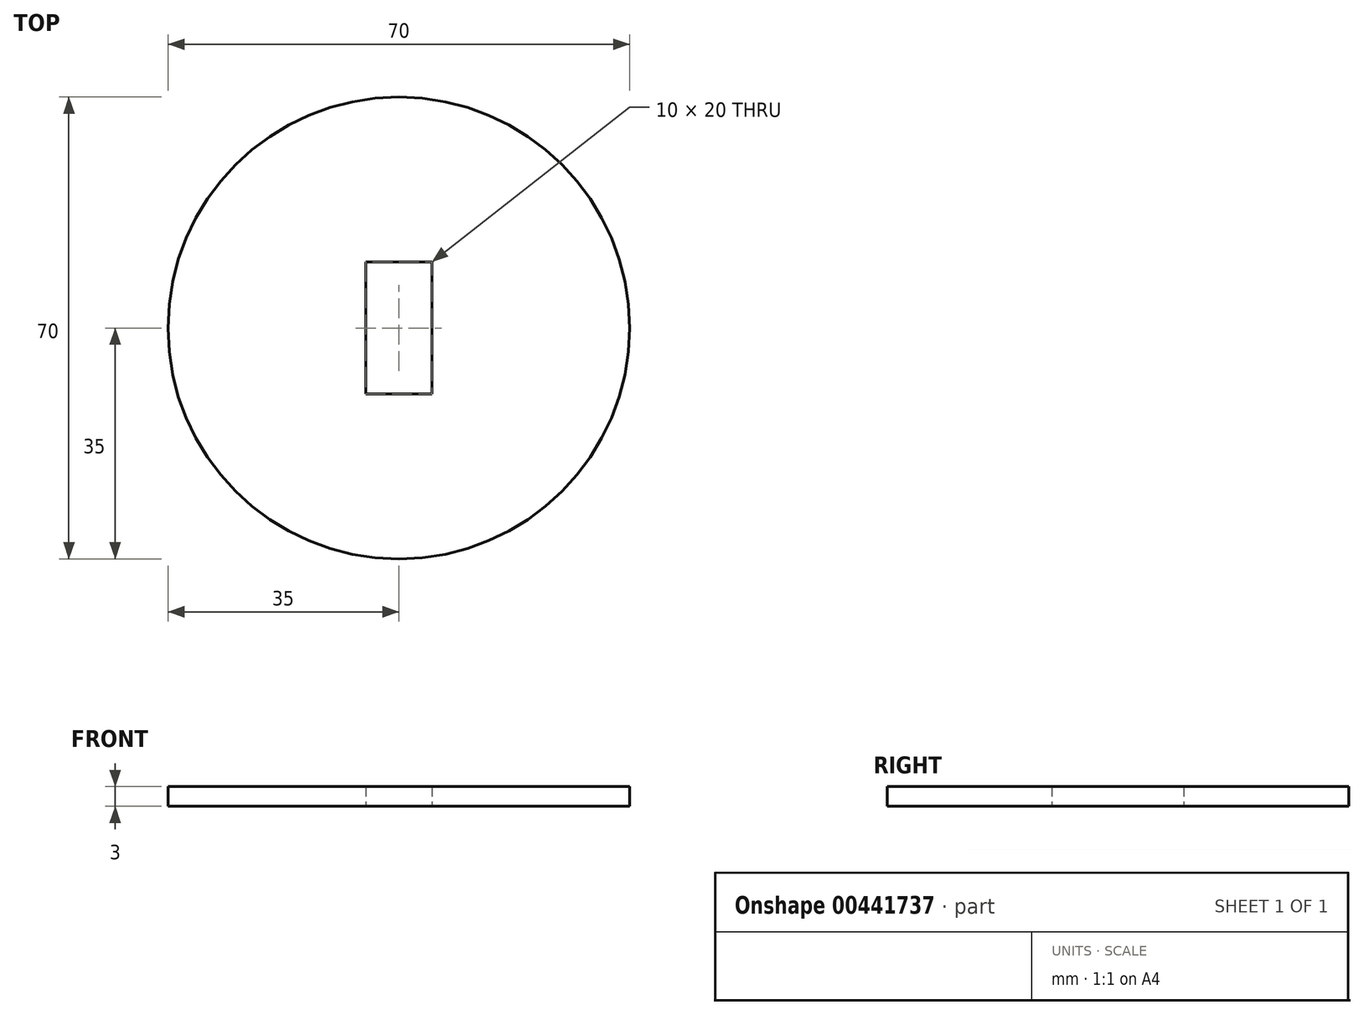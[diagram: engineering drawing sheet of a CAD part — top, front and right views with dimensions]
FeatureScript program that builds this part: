
annotation { "Feature Type Name" : "Feature", "Feature Type Description" : "" }
export const myFeature = defineFeature(function(context is Context, id is Id, definition is map)
    precondition{}
    {
        {
            var Q0;
            Q0=qCreatedBy(makeId("Top.planeOp"),FACE);
            var sketch = newSketch(context, id + "F0", { "sketchPlane" : qUnion([Q0])});
            skCircle(sketch, "E0", {"center": v(0, 0) * mm, "radius": 35 * mm});
            skLineSegment(sketch, "E1.bottom", {"start": v(-5, 10) * mm, "end": v(5, 10) * mm});
            skLineSegment(sketch, "E1.top", {"start": v(-5, -10) * mm, "end": v(5, -10) * mm});
            skLineSegment(sketch, "E1.left", {"start": v(-5, 10) * mm, "end": v(-5, -10) * mm});
            skLineSegment(sketch, "E1.right", {"start": v(5, 10) * mm, "end": v(5, -10) * mm});
            skLineSegment(sketch, "E2.bottom", {"start": v(5, 0) * mm, "end": v(5, 0) * mm});
            skLineSegment(sketch, "E2.top", {"start": v(5, 7.21) * mm, "end": v(5, 7.21) * mm});
            skLineSegment(sketch, "E2.left", {"start": v(5, 0) * mm, "end": v(5, 7.21) * mm});
            skLineSegment(sketch, "E2.right", {"start": v(5, 0) * mm, "end": v(5, 7.21) * mm});
            skPoint(sketch, "E2.middle", {"position": v(5, 3.6) * mm});
            skSolve(sketch);
        }
        {
            var Q0;
            Q0 = qSketchRegion(id + "F0", true);
            extrude(context, id + "F1", {"entities" : qUnion([Q0]), "depth" : 3 * mm});
        }
    });
